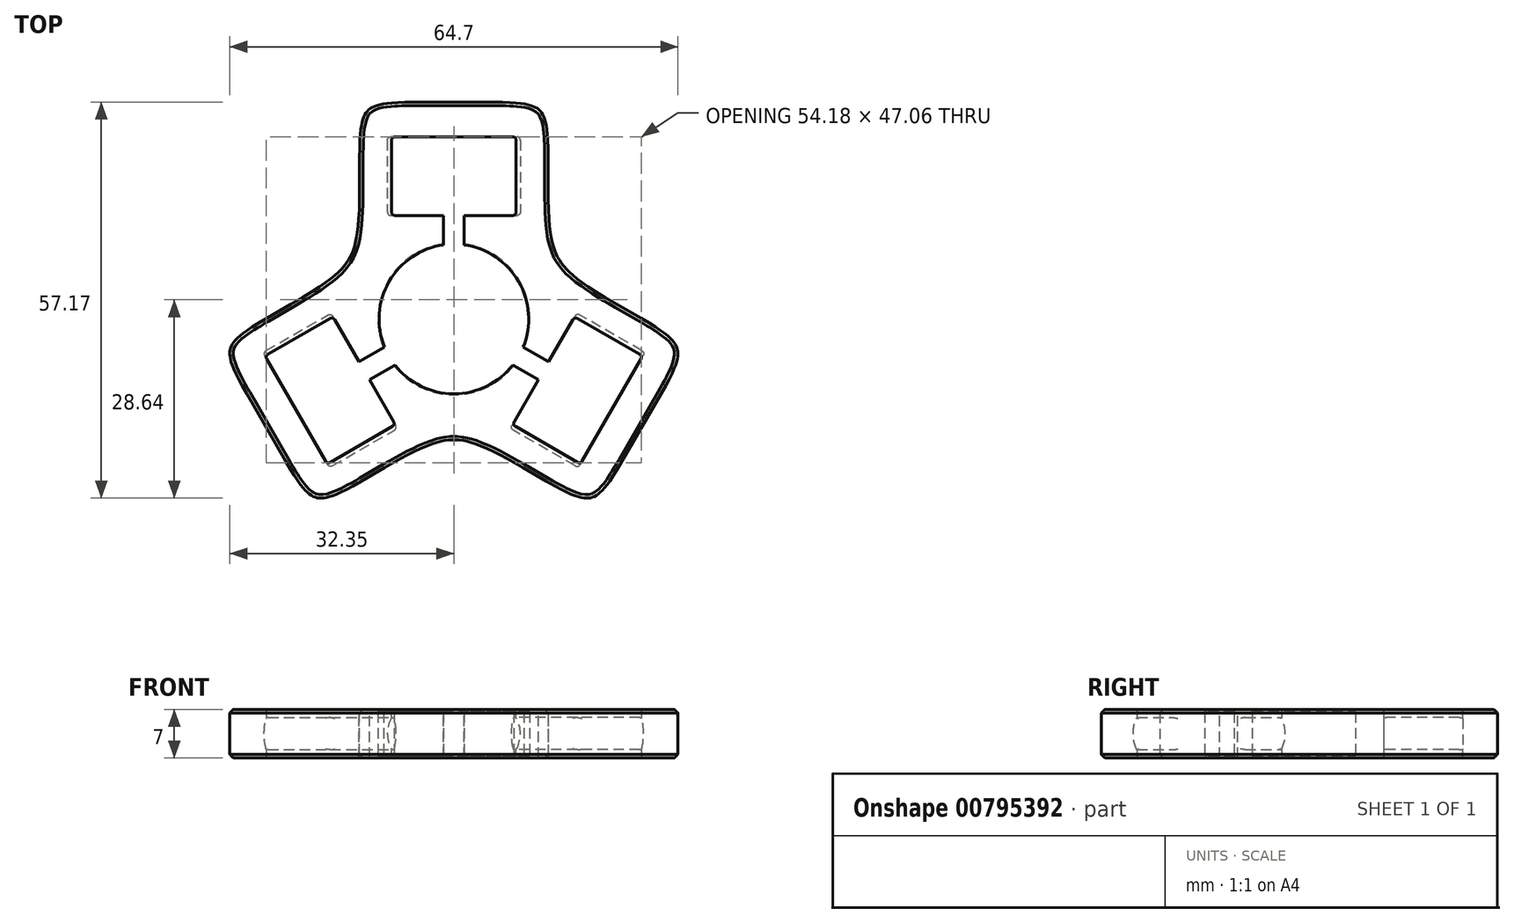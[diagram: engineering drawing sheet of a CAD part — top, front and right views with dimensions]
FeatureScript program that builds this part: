
annotation { "Feature Type Name" : "Feature", "Feature Type Description" : "" }
export const myFeature = defineFeature(function(context is Context, id is Id, definition is map)
    precondition{}
    {
        {
            var Q0;
            Q0=qCreatedBy(makeId("Top.planeOp"),FACE);
            var sketch = newSketch(context, id + "F0", { "sketchPlane" : qUnion([Q0])});
            skCircle(sketch, "E0", {"center": v(0, 0) * mm, "radius": 10.95 * mm});
            skLineSegment(sketch, "E1", {"start": v(0, 0) * mm, "end": v(0, 31.3) * mm});
            skLineSegment(sketch, "E2", {"start": v(0, 31.3) * mm, "end": v(13.6, 31.3) * mm});
            skLineSegment(sketch, "E3", {"start": v(0, 0) * mm, "end": v(13.6, 7.85) * mm});
            skLineSegment(sketch, "E4", {"start": v(0, 26.3) * mm, "end": v(9.6, 26.3) * mm, "construction": true});
            skLineSegment(sketch, "E5", {"start": v(9.6, 26.3) * mm, "end": v(9.6, 14.95) * mm, "construction": true});
            skLineSegment(sketch, "E6", {"start": v(9.6, 14.95) * mm, "end": v(0, 14.95) * mm, "construction": true});
            skPoint(sketch, "E7", {"position": v(0, 10.95) * mm});
            skLineSegment(sketch, "E8", {"start": v(13.6, 31.3) * mm, "end": v(13.6, 7.85) * mm});
            skSolve(sketch);
        }
        {
            var Q0;
            {var subQ4=sQuery(id+"F0.wireOp",EDGE,"E2");Q0=makeQuery(id+"F0.imprint","IMPRINT",FACE,{"disambiguationData":[TD([[makeQuery(id+"F0.imprint","IMPRINT",EDGE,{"derivedFrom":subQ4}),-1.0]])]});}
            extrude(context, id + "F1", {"entities" : qUnion([Q0]), "endBound" : BoundingType.SYMMETRIC, "depth" : 7 * mm, "offsetDistance" : 25 * mm});
        }
        {
            var Q0;
            Q0=qCreatedBy(makeId("Front.planeOp"),FACE);
            var Q1;
            Q1=sQuery(id+"F0.wireOp",VERTEX,"E6.end");
            cPlane(context, id + "F2", {"entities" : qUnion([Q0, Q1]), "cplaneType" : CPlaneType.PLANE_POINT, "offset" : 25 * mm, "width" : 150 * mm, "height" : 150 * mm});
        }
        {
            var Q0;
            Q0=qCreatedBy(id+"F2.planeOp",FACE);
            var sketch = newSketch(context, id + "F3", { "sketchPlane" : qUnion([Q0])});
            skCircle(sketch, "E9", {"center": v(4.8, 0) * mm, "radius": 4.8 * mm});
            skLineSegment(sketch, "E10", {"start": v(4.8, 4.8) * mm, "end": v(0, 4.8) * mm});
            skLineSegment(sketch, "E11", {"start": v(0, 4.8) * mm, "end": v(0, -4.8) * mm});
            skLineSegment(sketch, "E12", {"start": v(0, -4.8) * mm, "end": v(4.8, -4.8) * mm});
            skSolve(sketch);
        }
        {
            var Q0;
            Q0 = qSketchRegion(id + "F3", true);
            var Q1;
            Q1=sQuery(id+"F0.wireOp",VERTEX,"E4.start");
            extrude(context, id + "F4", {"entities" : qUnion([Q0]), "operationType" : NewBodyOperationType.REMOVE, "endBound" : BoundingType.UP_TO_VERTEX, "oppositeDirection" : true, "depth" : 25 * mm, "endBoundEntityVertex" : qUnion([Q1]), "offsetDistance" : 25 * mm});
        }
        {
            var Q0;
            Q0=makeQuery(id+"F1.opExtrude","SWEPT_EDGE",EDGE,{"disambiguationData":[OSD([sQuery(id+"F0.wireOp",EDGE,"E2"),sQuery(id+"F0.wireOp",EDGE,"E8")])]});
            fillet(context, id + "F5", {"entities" : qUnion([Q0]), "radius" : 8 * mm, "tangentPropagation" : true, "rho" : .7, "crossSection" : FilletCrossSection.CONIC, "allowEdgeOverflow" : false});
        }
        {
            var Q0;
            Q0=makeQuery(id+"F1.opExtrude","SWEPT_FACE",FACE,{"disambiguationData":[OSD([sQuery(id+"F0.wireOp",EDGE,"E3")])]});
            var sketch = newSketch(context, id + "F6", { "sketchPlane" : qUnion([Q0])});
            skLineSegment(sketch, "E13", {"start": v(10.95, 3.5) * mm, "end": v(10.95, 3.1) * mm});
            skLineSegment(sketch, "E14", {"start": v(10.95, 3.1) * mm, "end": v(10.8, 3.25) * mm});
            skLineSegment(sketch, "E15", {"start": v(10.8, 3.25) * mm, "end": v(10.8, 3.5) * mm});
            skLineSegment(sketch, "E16", {"start": v(10.8, 3.5) * mm, "end": v(10.95, 3.5) * mm});
            skLineSegment(sketch, "E17", {"start": v(10.95, -3.5) * mm, "end": v(10.8, -3.5) * mm});
            skLineSegment(sketch, "E18", {"start": v(10.8, -3.5) * mm, "end": v(10.8, -3.25) * mm});
            skLineSegment(sketch, "E19", {"start": v(10.8, -3.25) * mm, "end": v(10.95, -3.1) * mm});
            skLineSegment(sketch, "E20", {"start": v(10.95, -3.1) * mm, "end": v(10.95, -3.5) * mm});
            skSolve(sketch);
        }
        {
            var Q0;
            Q0 = qSketchRegion(id + "F6", true);
            var Q1;
            Q1=makeQuery(id+"F1.opExtrude","CAP_EDGE",EDGE,{"disambiguationData":[OSD([sQuery(id+"F0.wireOp",EDGE,"E0")])],"isStart":false});
            sweep(context, id + "F7", {"operationType" : NewBodyOperationType.ADD, "profiles" : qUnion([Q0]), "path" : qUnion([Q1])});
        }
        {
            var Q0;
            Q0=qCreatedBy(makeId("Top.planeOp"),FACE);
            var sketch = newSketch(context, id + "F8", { "sketchPlane" : qUnion([Q0])});
            skLineSegment(sketch, "E21.bottom", {"start": v(-1.5, 0) * mm, "end": v(1.5, 0) * mm});
            skLineSegment(sketch, "E21.top", {"start": v(-1.5, 14.95) * mm, "end": v(1.5, 14.95) * mm});
            skLineSegment(sketch, "E21.left", {"start": v(-1.5, 0) * mm, "end": v(-1.5, 14.95) * mm});
            skLineSegment(sketch, "E21.right", {"start": v(1.5, 0) * mm, "end": v(1.5, 14.95) * mm});
            skSolve(sketch);
        }
        {
            var Q0;
            Q0 = qSketchRegion(id + "F8", true);
            extrude(context, id + "F9", {"entities" : qUnion([Q0]), "operationType" : NewBodyOperationType.REMOVE, "endBound" : BoundingType.THROUGH_ALL, "oppositeDirection" : true, "depth" : 25 * mm, "offsetDistance" : 25 * mm, "hasSecondDirection" : true, "secondDirectionBound" : SecondDirectionBoundingType.THROUGH_ALL, "secondDirectionOppositeDirection" : false, "secondDirectionDepth" : 25 * mm});
        }
        {
            var Q0;
            Q0=qCreatedBy(makeId("Top.planeOp"),FACE);
            var sketch = newSketch(context, id + "F10", { "sketchPlane" : qUnion([Q0])});
            skLineSegment(sketch, "E22.bottom", {"start": v(0, 14.95) * mm, "end": v(9, 14.95) * mm});
            skLineSegment(sketch, "E22.top", {"start": v(0, 26.3) * mm, "end": v(9, 26.3) * mm});
            skLineSegment(sketch, "E22.left", {"start": v(0, 14.95) * mm, "end": v(0, 26.3) * mm});
            skLineSegment(sketch, "E22.right", {"start": v(9, 14.95) * mm, "end": v(9, 26.3) * mm});
            skLineSegment(sketch, "E23", {"start": v(9, 14.95) * mm, "end": v(9.6, 14.95) * mm, "construction": true});
            skSolve(sketch);
        }
        {
            var Q0;
            Q0 = qSketchRegion(id + "F10", true);
            extrude(context, id + "F11", {"entities" : qUnion([Q0]), "operationType" : NewBodyOperationType.REMOVE, "endBound" : BoundingType.THROUGH_ALL, "oppositeDirection" : true, "depth" : 25 * mm, "offsetDistance" : 25 * mm, "hasSecondDirection" : true, "secondDirectionBound" : SecondDirectionBoundingType.THROUGH_ALL, "secondDirectionOppositeDirection" : false, "secondDirectionDepth" : 25 * mm});
        }
        {
            var Q0;
            Q0=makeQuery(id+"F4.boolean.opBoolean","COPY",EDGE,{"derivedFrom":makeQuery(id+"F4.opExtrude","CAP_EDGE",EDGE,{"disambiguationData":[OSD([sQuery(id+"F3.wireOp",EDGE,"E9")])],"isStart":false})});
            var Q1;
            Q1=makeQuery(id+"F4.boolean.opBoolean","COPY",EDGE,{"derivedFrom":makeQuery(id+"F4.opExtrude","CAP_EDGE",EDGE,{"disambiguationData":[OSD([sQuery(id+"F3.wireOp",EDGE,"E9")])],"isStart":true})});
            var Q2;
            {var subQ0=sQuery(id+"F0.wireOp",EDGE,"E0");var subQ2=sQuery(id+"F10.wireOp",EDGE,"E22.bottom");var subQ3=sQuery(id+"F10.wireOp",EDGE,"E22.right");Q2=makeQuery(id+"F11.boolean.opBoolean","COPY",EDGE,{"disambiguationData":[TD([makeQuery(id+"F7.opSweep","SWEPT_FACE",FACE,{"disambiguationData":[OSD([subQ0,sQuery(id+"F6.wireOp",EDGE,"E16")])]})])],"derivedFrom":makeQuery(id+"F11.opExtrude","SWEPT_EDGE",EDGE,{"disambiguationData":[OSD([subQ2,subQ3])]})});}
            var Q3;
            {var subQ0=sQuery(id+"F0.wireOp",EDGE,"E0");var subQ2=sQuery(id+"F10.wireOp",EDGE,"E22.bottom");var subQ3=sQuery(id+"F10.wireOp",EDGE,"E22.right");Q3=makeQuery(id+"F11.boolean.opBoolean","COPY",EDGE,{"disambiguationData":[TD([makeQuery(id+"F7.opSweep","SWEPT_FACE",FACE,{"disambiguationData":[OSD([subQ0,sQuery(id+"F6.wireOp",EDGE,"E17")])]})])],"derivedFrom":makeQuery(id+"F11.opExtrude","SWEPT_EDGE",EDGE,{"disambiguationData":[OSD([subQ2,subQ3])]})});}
            var Q4;
            {var subQ0=sQuery(id+"F0.wireOp",EDGE,"E0");var subQ1=sQuery(id+"F10.wireOp",EDGE,"E22.right");var subQ2=sQuery(id+"F10.wireOp",EDGE,"E22.top");Q4=makeQuery(id+"F11.boolean.opBoolean","COPY",EDGE,{"disambiguationData":[TD([makeQuery(id+"F7.opSweep","SWEPT_FACE",FACE,{"disambiguationData":[OSD([subQ0,sQuery(id+"F6.wireOp",EDGE,"E16")])]})])],"derivedFrom":makeQuery(id+"F11.opExtrude","SWEPT_EDGE",EDGE,{"disambiguationData":[OSD([subQ2,subQ1])]})});}
            var Q5;
            {var subQ0=sQuery(id+"F0.wireOp",EDGE,"E0");var subQ1=sQuery(id+"F10.wireOp",EDGE,"E22.right");var subQ2=sQuery(id+"F10.wireOp",EDGE,"E22.top");Q5=makeQuery(id+"F11.boolean.opBoolean","COPY",EDGE,{"disambiguationData":[TD([makeQuery(id+"F7.opSweep","SWEPT_FACE",FACE,{"disambiguationData":[OSD([subQ0,sQuery(id+"F6.wireOp",EDGE,"E17")])]})])],"derivedFrom":makeQuery(id+"F11.opExtrude","SWEPT_EDGE",EDGE,{"disambiguationData":[OSD([subQ2,subQ1])]})});}
            fillet(context, id + "F12", {"entities" : qUnion([Q0, Q1, Q2, Q3, Q4, Q5]), "radius" : .5 * mm, "tangentPropagation" : true, "allowEdgeOverflow" : false});
        }
        {
            var Q0;
            Q0=makeQuery(id+"F1.opExtrude","SWEPT_BODY",BODY,{"disambiguationData":[OSD([sQuery(id+"F0.wireOp",EDGE,"E0"),sQuery(id+"F0.wireOp",EDGE,"E1"),sQuery(id+"F0.wireOp",EDGE,"E2"),sQuery(id+"F0.wireOp",EDGE,"E3"),sQuery(id+"F0.wireOp",EDGE,"e48c03e6-d634-43ae-9a82-f95fb8625b90")])]});
            var Q1;
            Q1=makeQuery(id+"F1.opExtrude","SWEPT_FACE",FACE,{"disambiguationData":[OSD([sQuery(id+"F0.wireOp",EDGE,"E3")])]});
            mirror(context, id + "F13", {"operationType" : NewBodyOperationType.ADD, "entities" : qUnion([Q0]), "mirrorPlane" : qUnion([Q1])});
        }
        {
            var Q0;
            {var subQ0=makeQuery(id+"F1.opExtrude","SWEPT_EDGE",EDGE,{"disambiguationData":[OSD([sQuery(id+"F0.wireOp",EDGE,"E3"),sQuery(id+"F0.wireOp",EDGE,"E8")])]});Q0=makeQuery(id+"F13.boolean.opBoolean","MERGE",EDGE,{"derivedFrom":[subQ0,makeQuery(id+"F13.opPattern","COPY",EDGE,{"derivedFrom":subQ0,"instanceName":"1"})]});}
            fillet(context, id + "F14", {"entities" : qUnion([Q0]), "radius" : 20 * mm, "tangentPropagation" : true, "rho" : .7, "crossSection" : FilletCrossSection.CONIC, "allowEdgeOverflow" : false});
        }
        {
            var Q0;
            Q0=qCreatedBy(makeId("Right.planeOp"),FACE);
            var sketch = newSketch(context, id + "F15", { "sketchPlane" : qUnion([Q0])});
            skLineSegment(sketch, "E24", {"start": v(0, 0) * mm, "end": v(0, 16.71) * mm, "construction": true});
            skSolve(sketch);
        }
        {
            var Q0;
            Q0=makeQuery(id+"F1.opExtrude","SWEPT_BODY",BODY,{"disambiguationData":[OSD([sQuery(id+"F0.wireOp",EDGE,"E0"),sQuery(id+"F0.wireOp",EDGE,"E1"),sQuery(id+"F0.wireOp",EDGE,"E2"),sQuery(id+"F0.wireOp",EDGE,"E3"),sQuery(id+"F0.wireOp",EDGE,"e48c03e6-d634-43ae-9a82-f95fb8625b90")])]});
            var Q1;
            Q1=sQuery(id+"F15.wireOp",EDGE,"E24");
            circularPattern(context, id + "F16", {"operationType" : NewBodyOperationType.ADD, "entities" : qUnion([Q0]), "axis" : qUnion([Q1]), "angle" : 360 * degree, "instanceCount" : 3, "equalSpace" : true});
        }
        {
            var Q0;
            {var subQ0=makeQuery(id+"F1.opExtrude","CAP_EDGE",EDGE,{"disambiguationData":[OSD([sQuery(id+"F0.wireOp",EDGE,"E2")])],"isStart":false});Q0=makeQuery(id+"F16.boolean.opBoolean","MERGE",EDGE,{"derivedFrom":[subQ0,makeQuery(id+"F16.opPattern","COPY",EDGE,{"derivedFrom":makeQuery(id+"F13.opPattern","COPY",EDGE,{"derivedFrom":subQ0,"instanceName":"1"}),"instanceName":"1"})]});}
            var Q1;
            {var subQ0=makeQuery(id+"F1.opExtrude","CAP_EDGE",EDGE,{"disambiguationData":[OSD([sQuery(id+"F0.wireOp",EDGE,"E2")])],"isStart":true});Q1=makeQuery(id+"F16.boolean.opBoolean","MERGE",EDGE,{"derivedFrom":[subQ0,makeQuery(id+"F16.opPattern","COPY",EDGE,{"derivedFrom":makeQuery(id+"F13.opPattern","COPY",EDGE,{"derivedFrom":subQ0,"instanceName":"1"}),"instanceName":"1"})]});}
            chamfer(context, id + "F17", {"entities" : qUnion([Q0, Q1]), "width" : .5 * mm, "tangentPropagation" : true});
        }
    });
